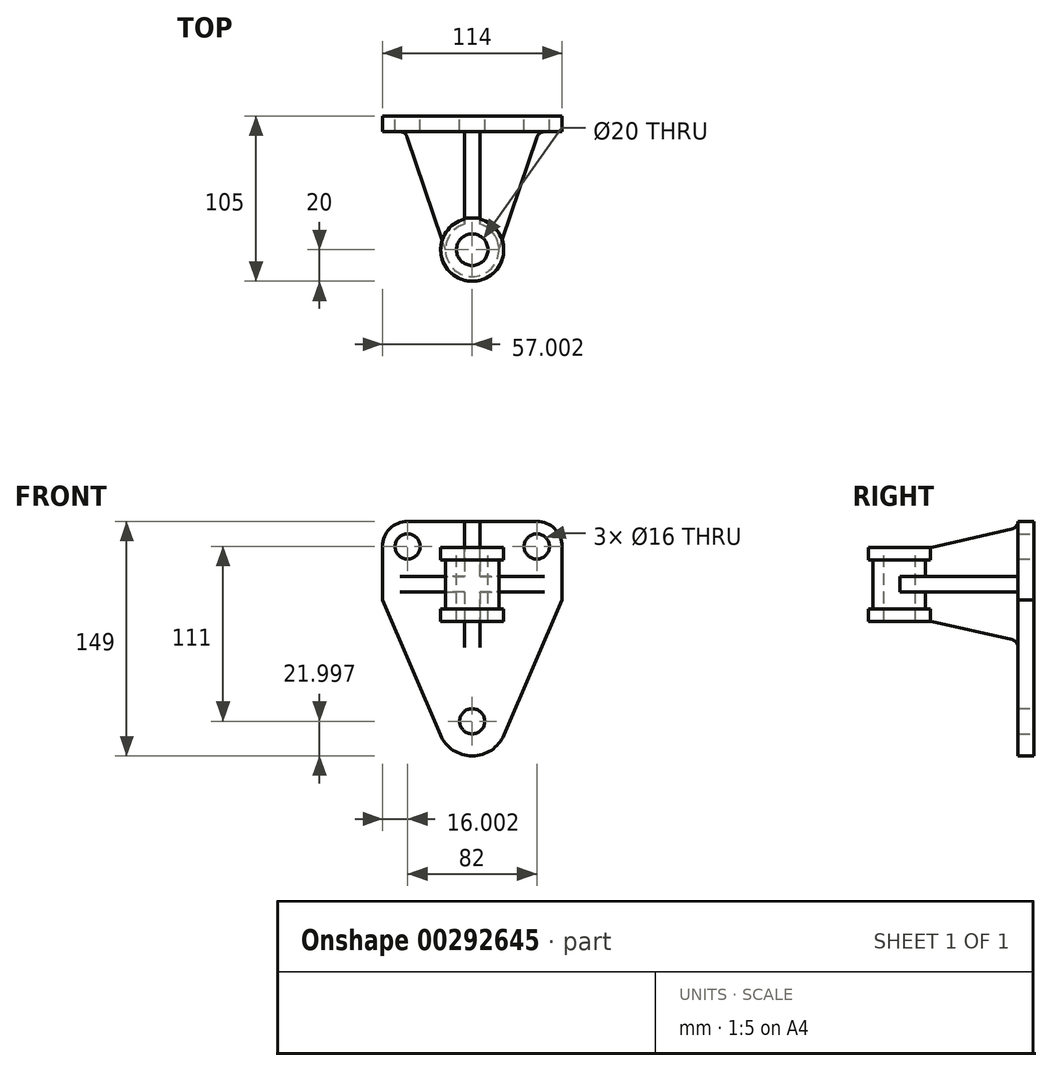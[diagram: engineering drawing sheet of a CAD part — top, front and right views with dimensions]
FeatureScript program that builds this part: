
annotation { "Feature Type Name" : "Feature", "Feature Type Description" : "" }
export const myFeature = defineFeature(function(context is Context, id is Id, definition is map)
    precondition{}
    {
        {
            var Q0;
            Q0=qCreatedBy(makeId("Front.planeOp"),FACE);
            var sketch = newSketch(context, id + "F0", { "sketchPlane" : qUnion([Q0])});
            skLineSegment(sketch, "E0", {"start": v(-54.95, 108) * mm, "end": v(59.05, 108) * mm});
            skLineSegment(sketch, "E1", {"start": v(59.05, 108) * mm, "end": v(59.05, 58) * mm});
            skLineSegment(sketch, "E2", {"start": v(-54.95, 108) * mm, "end": v(-54.95, 58) * mm});
            skPoint(sketch, "E3.orphan", {"position": v(2.05, 108) * mm});
            skPoint(sketch, "E4.orphan", {"position": v(2.05, -30) * mm});
            skPoint(sketch, "E5.end.orphan", {"position": v(2.05, -8) * mm});
            skArc(sketch, "E6", {"start": v(-18.16, -27.67) * mm, "mid": v(2.05, -41) * mm, "end": v(22.27, -27.67) * mm});
            skLineSegment(sketch, "E7", {"start": v(-54.95, 58) * mm, "end": v(-18.16, -27.67) * mm});
            skLineSegment(sketch, "E8", {"start": v(59.05, 58) * mm, "end": v(22.27, -27.67) * mm});
            skArc(sketch, "E9", {"start": v(22.27, -27.67) * mm, "mid": v(2.05, -41) * mm, "end": v(-18.16, -27.67) * mm});
            skCircle(sketch, "E10", {"center": v(2.05, -19) * mm, "radius": 8 * mm});
            skSolve(sketch);
        }
        {
            var Q0;
            Q0 = qSketchRegion(id + "F0", true);
            extrude(context, id + "F1", {"entities" : qUnion([Q0]), "depth" : 10 * mm});
        }
        {
            var Q0;
            Q0=makeQuery(id+"F1.opExtrude","SWEPT_EDGE",EDGE,{"disambiguationData":[OSD([sQuery(id+"F0.wireOp",EDGE,"E0"),sQuery(id+"F0.wireOp",EDGE,"E2")])]});
            var Q1;
            Q1=makeQuery(id+"F1.opExtrude","SWEPT_EDGE",EDGE,{"disambiguationData":[OSD([sQuery(id+"F0.wireOp",EDGE,"E0"),sQuery(id+"F0.wireOp",EDGE,"E1")])]});
            fillet(context, id + "F2", {"entities" : qUnion([Q0, Q1]), "radius" : 16 * mm, "tangentPropagation" : true, "allowEdgeOverflow" : false});
        }
        {
            var Q0;
            Q0=makeQuery(id+"F1.opExtrude","CAP_FACE",FACE,{"disambiguationData":[OSD([sQuery(id+"F0.wireOp",EDGE,"E0"),sQuery(id+"F0.wireOp",EDGE,"E1"),sQuery(id+"F0.wireOp",EDGE,"E2"),sQuery(id+"F0.wireOp",EDGE,"E7"),sQuery(id+"F0.wireOp",EDGE,"E8"),sQuery(id+"F0.wireOp",EDGE,"E9"),sQuery(id+"F0.wireOp",EDGE,"E10")])],"isStart":true});
            var sketch = newSketch(context, id + "F3", { "sketchPlane" : qUnion([Q0])});
            skCircle(sketch, "E11", {"center": v(-43.05, 92) * mm, "radius": 8 * mm});
            skCircle(sketch, "E12", {"center": v(38.95, 92) * mm, "radius": 8 * mm});
            skSolve(sketch);
        }
        {
            var Q0;
            Q0 = qSketchRegion(id + "F3", true);
            extrude(context, id + "F4", {"entities" : qUnion([Q0]), "operationType" : NewBodyOperationType.REMOVE, "endBound" : BoundingType.THROUGH_ALL, "oppositeDirection" : true, "depth" : 25 * mm});
        }
        {
            var Q0;
            Q0=makeQuery(id+"F1.opExtrude","CAP_FACE",FACE,{"disambiguationData":[OSD([sQuery(id+"F0.wireOp",EDGE,"E0"),sQuery(id+"F0.wireOp",EDGE,"E1"),sQuery(id+"F0.wireOp",EDGE,"E2"),sQuery(id+"F0.wireOp",EDGE,"E7"),sQuery(id+"F0.wireOp",EDGE,"E8"),sQuery(id+"F0.wireOp",EDGE,"E9"),sQuery(id+"F0.wireOp",EDGE,"E10")])],"isStart":false});
            var sketch = newSketch(context, id + "F5", { "sketchPlane" : qUnion([Q0])});
            skLineSegment(sketch, "E13", {"start": v(2.05, 108) * mm, "end": v(7.05, 108) * mm});
            skLineSegment(sketch, "E14", {"start": v(7.05, 108) * mm, "end": v(-2.95, 108) * mm});
            skLineSegment(sketch, "E15", {"start": v(-2.95, 108) * mm, "end": v(-2.95, 28) * mm});
            skLineSegment(sketch, "E16", {"start": v(-2.95, 28) * mm, "end": v(7.05, 28) * mm});
            skLineSegment(sketch, "E17", {"start": v(7.05, 28) * mm, "end": v(7.05, 108) * mm});
            skSolve(sketch);
        }
        {
            var Q0;
            Q0 = qSketchRegion(id + "F5", true);
            extrude(context, id + "F6", {"entities" : qUnion([Q0]), "operationType" : NewBodyOperationType.ADD, "depth" : 75 * mm});
        }
        {
            var Q0;
            Q0=makeQuery(id+"F6.opExtrude","SWEPT_FACE",FACE,{"disambiguationData":[OSD([sQuery(id+"F5.wireOp",EDGE,"E15")])]});
            var sketch = newSketch(context, id + "F7", { "sketchPlane" : qUnion([Q0])});
            skArc(sketch, "E18", {"start": v(10, 108) * mm, "mid": v(11.1, 104.89) * mm, "end": v(13.9, 103.13) * mm});
            skLineSegment(sketch, "E19", {"start": v(10, 108) * mm, "end": v(10, 68) * mm});
            skLineSegment(sketch, "E20", {"start": v(10, 68) * mm, "end": v(85, 68) * mm});
            skLineSegment(sketch, "E21", {"start": v(85, 68) * mm, "end": v(85, 87) * mm});
            skLineSegment(sketch, "E22", {"start": v(65, 91.54) * mm, "end": v(13.9, 103.13) * mm});
            skLineSegment(sketch, "E23", {"start": v(85, 91.54) * mm, "end": v(65, 91.54) * mm});
            skLineSegment(sketch, "E24", {"start": v(85, 91.54) * mm, "end": v(85, 87) * mm});
            skLineSegment(sketch, "E25.MirrorCS", {"start": v(85, 68) * mm, "end": v(85, 49) * mm});
            skLineSegment(sketch, "E26.MirrorCS", {"start": v(85, 44.47) * mm, "end": v(85, 49) * mm});
            skLineSegment(sketch, "E27.MirrorCS", {"start": v(85, 44.47) * mm, "end": v(65, 44.47) * mm});
            skLineSegment(sketch, "E28.MirrorCS", {"start": v(65, 44.47) * mm, "end": v(13.9, 32.88) * mm});
            skArc(sketch, "E29.MirrorCS", {"start": v(10, 28) * mm, "mid": v(11.1, 31.13) * mm, "end": v(13.9, 32.88) * mm});
            skLineSegment(sketch, "E30", {"start": v(10, 108) * mm, "end": v(85, 108) * mm});
            skLineSegment(sketch, "E31", {"start": v(85, 108) * mm, "end": v(85, 28) * mm});
            skLineSegment(sketch, "E32", {"start": v(85, 28) * mm, "end": v(10, 28) * mm});
            skSolve(sketch);
        }
        {
            var Q0;
            Q0=makeQuery(id+"F7.imprint","IMPRINT",FACE,{"disambiguationData":[TD([[makeQuery(id+"F7.imprint","IMPRINT",EDGE,{"derivedFrom":sQuery(id+"F7.wireOp",EDGE,"E18")}),1.0]])]});
            var Q1;
            {var subQ2=sQuery(id+"F7.wireOp",EDGE,"E27.MirrorCS");Q1=makeQuery(id+"F7.imprint","IMPRINT",FACE,{"disambiguationData":[TD([[makeQuery(id+"F7.imprint","IMPRINT",EDGE,{"derivedFrom":subQ2}),1.0]])]});}
            extrude(context, id + "F8", {"entities" : qUnion([Q0, Q1]), "operationType" : NewBodyOperationType.REMOVE, "endBound" : BoundingType.THROUGH_ALL, "oppositeDirection" : true, "depth" : 25 * mm});
        }
        {
            var Q0;
            Q0=makeQuery(id+"F8.boolean.opBoolean","COPY",FACE,{"derivedFrom":makeQuery(id+"F8.opExtrude","SWEPT_FACE",FACE,{"disambiguationData":[OSD([sQuery(id+"F7.wireOp",EDGE,"E23")])]})});
            var sketch = newSketch(context, id + "F9", { "sketchPlane" : qUnion([Q0])});
            skCircle(sketch, "E33", {"center": v(2.05, -85) * mm, "radius": 20 * mm});
            skSolve(sketch);
        }
        {
            var Q0;
            Q0 = qSketchRegion(id + "F9", true);
            extrude(context, id + "F10", {"entities" : qUnion([Q0]), "operationType" : NewBodyOperationType.ADD, "oppositeDirection" : true, "depth" : 8 * mm});
        }
        {
            var Q0;
            Q0=makeQuery(id+"F8.boolean.opBoolean","COPY",FACE,{"derivedFrom":makeQuery(id+"F8.opExtrude","SWEPT_FACE",FACE,{"disambiguationData":[OSD([sQuery(id+"F7.wireOp",EDGE,"E27.MirrorCS")])]})});
            var sketch = newSketch(context, id + "F11", { "sketchPlane" : qUnion([Q0])});
            skCircle(sketch, "E34", {"center": v(2.05, 85) * mm, "radius": 20 * mm});
            skSolve(sketch);
        }
        {
            var Q0;
            Q0 = qSketchRegion(id + "F11", true);
            extrude(context, id + "F12", {"entities" : qUnion([Q0]), "operationType" : NewBodyOperationType.ADD, "oppositeDirection" : true, "depth" : 8 * mm});
        }
        {
            var Q0;
            Q0=makeQuery(id+"F12.opExtrude","CAP_FACE",FACE,{"disambiguationData":[OSD([sQuery(id+"F11.wireOp",EDGE,"E34")])],"isStart":false});
            var sketch = newSketch(context, id + "F13", { "sketchPlane" : qUnion([Q0])});
            skCircle(sketch, "E35", {"center": v(2.05, -85) * mm, "radius": 17 * mm});
            skPoint(sketch, "E35.perimeterSnap0", {"position": v(2.05, -85) * mm});
            skPoint(sketch, "E35.perimeterSnap1", {"position": v(-2.95, -75.32) * mm});
            skSolve(sketch);
        }
        {
            var Q0;
            Q0 = qSketchRegion(id + "F13", true);
            extrude(context, id + "F14", {"entities" : qUnion([Q0]), "operationType" : NewBodyOperationType.ADD, "depth" : 38 * mm});
        }
        {
            var Q0;
            Q0=makeQuery(id+"F10.boolean.opBoolean","MERGE",FACE,{"derivedFrom":[makeQuery(id+"F8.boolean.opBoolean","COPY",FACE,{"derivedFrom":makeQuery(id+"F8.opExtrude","SWEPT_FACE",FACE,{"disambiguationData":[OSD([sQuery(id+"F7.wireOp",EDGE,"E23")])]})}),makeQuery(id+"F10.opExtrude","CAP_FACE",FACE,{"disambiguationData":[OSD([sQuery(id+"F9.wireOp",EDGE,"E33")])],"isStart":true})]});
            var sketch = newSketch(context, id + "F15", { "sketchPlane" : qUnion([Q0])});
            skCircle(sketch, "E36", {"center": v(2.05, -85) * mm, "radius": 10 * mm});
            skSolve(sketch);
        }
        {
            var Q0;
            Q0 = qSketchRegion(id + "F15", true);
            extrude(context, id + "F16", {"entities" : qUnion([Q0]), "operationType" : NewBodyOperationType.REMOVE, "endBound" : BoundingType.THROUGH_ALL, "oppositeDirection" : true, "depth" : 25 * mm});
        }
        {
            var Q0;
            Q0=makeQuery(id+"F1.opExtrude","CAP_FACE",FACE,{"disambiguationData":[OSD([sQuery(id+"F0.wireOp",EDGE,"E0"),sQuery(id+"F0.wireOp",EDGE,"E1"),sQuery(id+"F0.wireOp",EDGE,"E2"),sQuery(id+"F0.wireOp",EDGE,"E7"),sQuery(id+"F0.wireOp",EDGE,"E8"),sQuery(id+"F0.wireOp",EDGE,"E9"),sQuery(id+"F0.wireOp",EDGE,"E10")])],"isStart":false});
            var sketch = newSketch(context, id + "F17", { "sketchPlane" : qUnion([Q0])});
            skLineSegment(sketch, "E37", {"start": v(-43.95, 68) * mm, "end": v(-43.95, 73) * mm});
            skLineSegment(sketch, "E38", {"start": v(-43.95, 73) * mm, "end": v(-14.95, 73) * mm});
            skLineSegment(sketch, "E39", {"start": v(-14.95, 73) * mm, "end": v(-14.95, 63) * mm});
            skLineSegment(sketch, "E40", {"start": v(-14.95, 63) * mm, "end": v(-43.95, 63) * mm});
            skLineSegment(sketch, "E41", {"start": v(-43.95, 63) * mm, "end": v(-43.95, 73) * mm});
            skLineSegment(sketch, "E42.MirrorCS", {"start": v(48.05, 63) * mm, "end": v(48.05, 73) * mm});
            skLineSegment(sketch, "E43.MirrorCS", {"start": v(48.05, 73) * mm, "end": v(19.05, 73) * mm});
            skLineSegment(sketch, "E44.MirrorCS", {"start": v(19.05, 63) * mm, "end": v(48.05, 63) * mm});
            skPoint(sketch, "E45.start.orphan", {"position": v(2.05, 28) * mm});
            skPoint(sketch, "E46.start.orphan", {"position": v(-2.95, 68) * mm});
            skLineSegment(sketch, "E47", {"start": v(19.05, 63) * mm, "end": v(7.05, 63) * mm});
            skLineSegment(sketch, "E48", {"start": v(7.05, 63) * mm, "end": v(7.05, 73) * mm});
            skLineSegment(sketch, "E49", {"start": v(7.05, 73) * mm, "end": v(19.05, 73) * mm});
            skLineSegment(sketch, "E50", {"start": v(-14.95, 63) * mm, "end": v(-2.95, 63) * mm});
            skLineSegment(sketch, "E51", {"start": v(-2.95, 63) * mm, "end": v(-2.95, 73) * mm});
            skLineSegment(sketch, "E52", {"start": v(-2.95, 73) * mm, "end": v(-14.95, 73) * mm});
            skSolve(sketch);
        }
        {
            var Q0;
            Q0 = qSketchRegion(id + "F17", true);
            extrude(context, id + "F18", {"entities" : qUnion([Q0]), "operationType" : NewBodyOperationType.ADD, "depth" : 75 * mm});
        }
        {
            var Q0;
            {var subQ1=sQuery(id+"F17.wireOp",EDGE,"E49");var subQ2=sQuery(id+"F17.wireOp",EDGE,"E43.MirrorCS");Q0=makeQuery(id+"F18.boolean.opBoolean","SPLIT",FACE,{"disambiguationData":[TD([makeQuery(id+"F6.opExtrude","SWEPT_FACE",FACE,{"disambiguationData":[OSD([sQuery(id+"F5.wireOp",EDGE,"E17")])]})])],"derivedFrom":makeQuery(id+"F18.opExtrude","SWEPT_FACE",FACE,{"disambiguationData":[OSD([subQ2,subQ1])]})});}
            var sketch = newSketch(context, id + "F19", { "sketchPlane" : qUnion([Q0])});
            skCircle(sketch, "E53", {"center": v(2.05, -85) * mm, "radius": 10 * mm});
            skSolve(sketch);
        }
        {
            var Q0;
            Q0 = qSketchRegion(id + "F19", true);
            extrude(context, id + "F20", {"entities" : qUnion([Q0]), "operationType" : NewBodyOperationType.REMOVE, "endBound" : BoundingType.THROUGH_ALL, "oppositeDirection" : true, "depth" : 25 * mm});
        }
        {
            var Q0;
            {var subQ1=sQuery(id+"F17.wireOp",EDGE,"E49");var subQ2=sQuery(id+"F17.wireOp",EDGE,"E43.MirrorCS");Q0=makeQuery(id+"F18.boolean.opBoolean","SPLIT",FACE,{"disambiguationData":[TD([makeQuery(id+"F6.opExtrude","SWEPT_FACE",FACE,{"disambiguationData":[OSD([sQuery(id+"F5.wireOp",EDGE,"E17")])]})])],"derivedFrom":makeQuery(id+"F18.opExtrude","SWEPT_FACE",FACE,{"disambiguationData":[OSD([subQ2,subQ1])]})});}
            var sketch = newSketch(context, id + "F21", { "sketchPlane" : qUnion([Q0])});
            skArc(sketch, "E54", {"start": v(48.05, -10) * mm, "mid": v(45.14, -10.94) * mm, "end": v(43.32, -13.4) * mm});
            skLineSegment(sketch, "E55", {"start": v(19.05, -85) * mm, "end": v(43.32, -13.4) * mm});
            skLineSegment(sketch, "E56", {"start": v(19.05, -85) * mm, "end": v(48.05, -85) * mm});
            skLineSegment(sketch, "E57", {"start": v(48.05, -85) * mm, "end": v(48.05, -10) * mm});
            skLineSegment(sketch, "E58.MirrorCS", {"start": v(-14.95, -85) * mm, "end": v(-39.21, -13.4) * mm});
            skArc(sketch, "E59.MirrorC", {"start": v(-43.95, -10) * mm, "mid": v(-41.03, -10.94) * mm, "end": v(-39.21, -13.4) * mm});
            skLineSegment(sketch, "E60.MirrorCS", {"start": v(-43.95, -85) * mm, "end": v(-43.95, -10) * mm});
            skLineSegment(sketch, "E61.MirrorCS", {"start": v(-14.95, -85) * mm, "end": v(-43.95, -85) * mm});
            skPoint(sketch, "E62.start.orphan", {"position": v(2.05, -85) * mm});
            skSolve(sketch);
        }
        {
            var Q0;
            Q0 = qSketchRegion(id + "F21", true);
            extrude(context, id + "F22", {"entities" : qUnion([Q0]), "operationType" : NewBodyOperationType.REMOVE, "oppositeDirection" : true, "depth" : 10 * mm});
        }
    });
